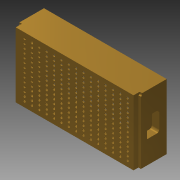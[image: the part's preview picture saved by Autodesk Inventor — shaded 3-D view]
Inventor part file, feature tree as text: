
AUTODESK INVENTOR PART (.ipt)
format: ipt  version: 2015 (Build 190159000, 159)  size: 348,672 bytes
history: native  units: mm
features: extrude x5, sketch x5, pattern_linear x3, fillet x1, shell x1
ambient origin geometry x8: Origin, YZ Plane, XZ Plane, XY Plane, X Axis, Y Axis, Z Axis, Center Point
bodies: 实体1 (feature_tree)
feature tree (15):
  extrude  "拉伸1"  Depth=500.0mm
  extrude  "拉伸2"  Depth=10.0mm
  extrude  "拉伸3"  Depth=265.0mm TaperAngle=0.0deg
  extrude  "拉伸4"  Depth=10.0mm TaperAngle=0.0deg
  fillet  "圆角1"  Radius=10.0mm
  pattern_linear  "矩形阵列1"  Count1=8  [1 undecoded]
  shell  "抽壳1"  Thickness=50.0mm
  extrude  "拉伸5"  Depth=92.5mm
  pattern_linear  "矩形阵列2"  Count1=3  [1 undecoded]
  pattern_linear  "矩形阵列3"  Count1=3 Spacing1=0.0mm
  sketch  "草图1"  dims[d0=105.0mm d1=500.0mm]
  sketch  "草图2"  dims[d2=10.0mm d3=10.0mm]
  sketch  "草图3"  dims[d4=20.0mm d5=265.0mm d6=0.0mm]
  sketch  "草图4"  dims[d7=5.0mm d8=10.0mm d9=0.0mm d10=10.0mm]
  sketch  "草图5"  dims[d11=10.0mm d12=0.0mm d13=80.0mm d14=50.0mm d15=92.5mm d16=30.0mm d17=30.0mm d18=0.0mm d19=10.0mm d20=20.0mm d22=470.0mm d23=5.0mm d24=10.0mm d25=30.0mm d26=17.0mm d27=5.0mm d28=0.0mm d29=150.0mm d31=30.0mm d32=140.0mm d34=17.0mm]
note: 2 required parameter values undecoded (feature->parameter linkage not recoverable at this tier; creation-order binding heuristic only, values carry confidence <= 0.55)
